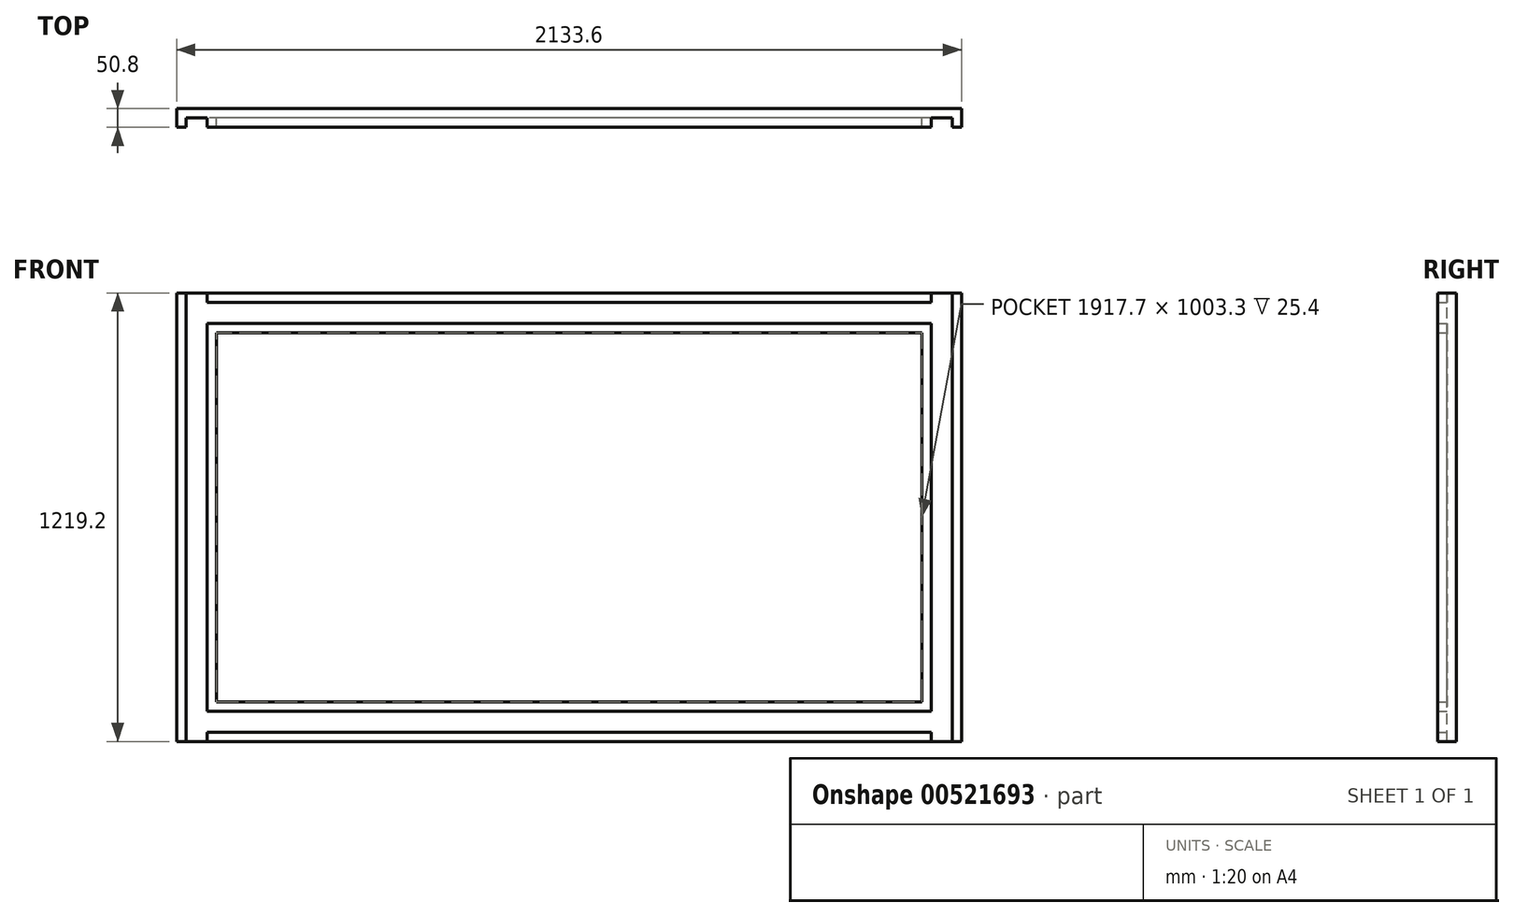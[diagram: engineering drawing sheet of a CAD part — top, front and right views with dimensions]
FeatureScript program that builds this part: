
annotation { "Feature Type Name" : "Feature", "Feature Type Description" : "" }
export const myFeature = defineFeature(function(context is Context, id is Id, definition is map)
    precondition{}
    {
        {
            var Q0;
            Q0=qCreatedBy(makeId("Front.planeOp"),FACE);
            var sketch = newSketch(context, id + "F0", { "sketchPlane" : qUnion([Q0])});
            skLineSegment(sketch, "E0.bottom", {"start": v(0, 0) * mm, "end": v(2133.6, 0) * mm});
            skLineSegment(sketch, "E0.top", {"start": v(0, 1219.2) * mm, "end": v(2133.6, 1219.2) * mm});
            skLineSegment(sketch, "E0.left", {"start": v(0, 0) * mm, "end": v(0, 1219.2) * mm});
            skLineSegment(sketch, "E0.right", {"start": v(2133.6, 0) * mm, "end": v(2133.6, 1219.2) * mm});
            skSolve(sketch);
        }
        {
            var Q0;
            Q0 = qSketchRegion(id + "F0", true);
            extrude(context, id + "F1", {"entities" : qUnion([Q0]), "depth" : 25.4 * mm, "offsetDistance" : 25.4 * mm});
        }
        {
            var Q0;
            Q0=makeQuery(id+"F1.opExtrude","CAP_FACE",FACE,{"disambiguationData":[OSD([sQuery(id+"F0.wireOp",EDGE,"E0.bottom"),sQuery(id+"F0.wireOp",EDGE,"E0.top"),sQuery(id+"F0.wireOp",EDGE,"E0.left"),sQuery(id+"F0.wireOp",EDGE,"E0.right")])],"isStart":false});
            var sketch = newSketch(context, id + "F2", { "sketchPlane" : qUnion([Q0])});
            skLineSegment(sketch, "E1.bottom", {"start": v(2051.05, 1219.2) * mm, "end": v(82.55, 1219.2) * mm});
            skLineSegment(sketch, "E1.top", {"start": v(2051.05, 1193.8) * mm, "end": v(82.55, 1193.8) * mm});
            skLineSegment(sketch, "E1.left", {"start": v(2051.05, 1219.2) * mm, "end": v(2051.05, 1193.8) * mm});
            skLineSegment(sketch, "E1.right", {"start": v(82.55, 1219.2) * mm, "end": v(82.55, 1193.8) * mm});
            skSolve(sketch);
        }
        {
            var Q0;
            Q0 = qSketchRegion(id + "F2", true);
            extrude(context, id + "F3", {"entities" : qUnion([Q0]), "operationType" : NewBodyOperationType.ADD, "depth" : 25.4 * mm, "offsetDistance" : 25.4 * mm});
        }
        {
            var Q0;
            Q0=makeQuery(id+"F1.opExtrude","CAP_FACE",FACE,{"disambiguationData":[OSD([sQuery(id+"F0.wireOp",EDGE,"E0.bottom"),sQuery(id+"F0.wireOp",EDGE,"E0.top"),sQuery(id+"F0.wireOp",EDGE,"E0.left"),sQuery(id+"F0.wireOp",EDGE,"E0.right")])],"isStart":false});
            var sketch = newSketch(context, id + "F4", { "sketchPlane" : qUnion([Q0])});
            skLineSegment(sketch, "E2.bottom", {"start": v(82.55, 0) * mm, "end": v(2051.05, 0) * mm});
            skLineSegment(sketch, "E2.top", {"start": v(82.55, 25.4) * mm, "end": v(2051.05, 25.4) * mm});
            skLineSegment(sketch, "E2.left", {"start": v(82.55, 0) * mm, "end": v(82.55, 25.4) * mm});
            skLineSegment(sketch, "E2.right", {"start": v(2051.05, 0) * mm, "end": v(2051.05, 25.4) * mm});
            skSolve(sketch);
        }
        {
            var Q0;
            Q0 = qSketchRegion(id + "F4", true);
            extrude(context, id + "F5", {"entities" : qUnion([Q0]), "operationType" : NewBodyOperationType.ADD, "depth" : 25.4 * mm, "offsetDistance" : 25.4 * mm});
        }
        {
            var Q0;
            Q0=makeQuery(id+"F1.opExtrude","CAP_FACE",FACE,{"disambiguationData":[OSD([sQuery(id+"F0.wireOp",EDGE,"E0.bottom"),sQuery(id+"F0.wireOp",EDGE,"E0.top"),sQuery(id+"F0.wireOp",EDGE,"E0.left"),sQuery(id+"F0.wireOp",EDGE,"E0.right")])],"isStart":false});
            var sketch = newSketch(context, id + "F6", { "sketchPlane" : qUnion([Q0])});
            skLineSegment(sketch, "E3.bottom", {"start": v(0, 1219.2) * mm, "end": v(25.4, 1219.2) * mm});
            skLineSegment(sketch, "E3.top", {"start": v(0, 0) * mm, "end": v(25.4, 0) * mm});
            skLineSegment(sketch, "E3.left", {"start": v(0, 1219.2) * mm, "end": v(0, 0) * mm});
            skLineSegment(sketch, "E3.right", {"start": v(25.4, 1219.2) * mm, "end": v(25.4, 0) * mm});
            skSolve(sketch);
        }
        {
            var Q0;
            Q0 = qSketchRegion(id + "F6", true);
            extrude(context, id + "F7", {"entities" : qUnion([Q0]), "operationType" : NewBodyOperationType.ADD, "depth" : 25.4 * mm, "offsetDistance" : 25.4 * mm});
        }
        {
            var Q0;
            Q0=makeQuery(id+"F1.opExtrude","CAP_FACE",FACE,{"disambiguationData":[OSD([sQuery(id+"F0.wireOp",EDGE,"E0.bottom"),sQuery(id+"F0.wireOp",EDGE,"E0.top"),sQuery(id+"F0.wireOp",EDGE,"E0.left"),sQuery(id+"F0.wireOp",EDGE,"E0.right")])],"isStart":false});
            var sketch = newSketch(context, id + "F8", { "sketchPlane" : qUnion([Q0])});
            skLineSegment(sketch, "E4.bottom", {"start": v(2133.6, 0) * mm, "end": v(2108.2, 0) * mm});
            skLineSegment(sketch, "E4.top", {"start": v(2133.6, 1219.2) * mm, "end": v(2108.2, 1219.2) * mm});
            skLineSegment(sketch, "E4.left", {"start": v(2133.6, 0) * mm, "end": v(2133.6, 1219.2) * mm});
            skLineSegment(sketch, "E4.right", {"start": v(2108.2, 0) * mm, "end": v(2108.2, 1219.2) * mm});
            skSolve(sketch);
        }
        {
            var Q0;
            Q0 = qSketchRegion(id + "F8", true);
            extrude(context, id + "F9", {"entities" : qUnion([Q0]), "operationType" : NewBodyOperationType.ADD, "depth" : 25.4 * mm, "offsetDistance" : 25.4 * mm});
        }
        {
            var Q0;
            Q0=makeQuery(id+"F1.opExtrude","CAP_FACE",FACE,{"disambiguationData":[OSD([sQuery(id+"F0.wireOp",EDGE,"E0.bottom"),sQuery(id+"F0.wireOp",EDGE,"E0.top"),sQuery(id+"F0.wireOp",EDGE,"E0.left"),sQuery(id+"F0.wireOp",EDGE,"E0.right")])],"isStart":false});
            var sketch = newSketch(context, id + "F10", { "sketchPlane" : qUnion([Q0])});
            skLineSegment(sketch, "E5.bottom", {"start": v(2051.05, 1136.65) * mm, "end": v(82.55, 1136.65) * mm});
            skLineSegment(sketch, "E5.top", {"start": v(2051.05, 1111.25) * mm, "end": v(82.55, 1111.25) * mm});
            skLineSegment(sketch, "E5.left", {"start": v(2051.05, 1136.65) * mm, "end": v(2051.05, 1111.25) * mm});
            skLineSegment(sketch, "E5.right", {"start": v(82.55, 1136.65) * mm, "end": v(82.55, 1111.25) * mm});
            skSolve(sketch);
        }
        {
            var Q0;
            Q0 = qSketchRegion(id + "F10", true);
            extrude(context, id + "F11", {"entities" : qUnion([Q0]), "operationType" : NewBodyOperationType.ADD, "depth" : 25.4 * mm, "offsetDistance" : 25.4 * mm});
        }
        {
            var Q0;
            Q0=makeQuery(id+"F1.opExtrude","CAP_FACE",FACE,{"disambiguationData":[OSD([sQuery(id+"F0.wireOp",EDGE,"E0.bottom"),sQuery(id+"F0.wireOp",EDGE,"E0.top"),sQuery(id+"F0.wireOp",EDGE,"E0.left"),sQuery(id+"F0.wireOp",EDGE,"E0.right")])],"isStart":false});
            var sketch = newSketch(context, id + "F12", { "sketchPlane" : qUnion([Q0])});
            skLineSegment(sketch, "E6.bottom", {"start": v(82.55, 82.55) * mm, "end": v(2051.05, 82.55) * mm});
            skLineSegment(sketch, "E6.top", {"start": v(82.55, 107.95) * mm, "end": v(2051.05, 107.95) * mm});
            skLineSegment(sketch, "E6.left", {"start": v(82.55, 82.55) * mm, "end": v(82.55, 107.95) * mm});
            skLineSegment(sketch, "E6.right", {"start": v(2051.05, 82.55) * mm, "end": v(2051.05, 107.95) * mm});
            skSolve(sketch);
        }
        {
            var Q0;
            Q0 = qSketchRegion(id + "F12", true);
            extrude(context, id + "F13", {"entities" : qUnion([Q0]), "operationType" : NewBodyOperationType.ADD, "depth" : 25.4 * mm, "offsetDistance" : 25.4 * mm});
        }
        {
            var Q0;
            Q0=makeQuery(id+"F1.opExtrude","CAP_FACE",FACE,{"disambiguationData":[OSD([sQuery(id+"F0.wireOp",EDGE,"E0.bottom"),sQuery(id+"F0.wireOp",EDGE,"E0.top"),sQuery(id+"F0.wireOp",EDGE,"E0.left"),sQuery(id+"F0.wireOp",EDGE,"E0.right")])],"isStart":false});
            var sketch = newSketch(context, id + "F14", { "sketchPlane" : qUnion([Q0])});
            skLineSegment(sketch, "E7.bottom", {"start": v(2051.05, 107.95) * mm, "end": v(2025.65, 107.95) * mm});
            skLineSegment(sketch, "E7.top", {"start": v(2051.05, 1111.25) * mm, "end": v(2025.65, 1111.25) * mm});
            skLineSegment(sketch, "E7.left", {"start": v(2051.05, 107.95) * mm, "end": v(2051.05, 1111.25) * mm});
            skLineSegment(sketch, "E7.right", {"start": v(2025.65, 107.95) * mm, "end": v(2025.65, 1111.25) * mm});
            skSolve(sketch);
        }
        {
            var Q0;
            Q0 = qSketchRegion(id + "F14", true);
            extrude(context, id + "F15", {"entities" : qUnion([Q0]), "operationType" : NewBodyOperationType.ADD, "depth" : 25.4 * mm, "offsetDistance" : 25.4 * mm});
        }
        {
            var Q0;
            Q0=makeQuery(id+"F1.opExtrude","CAP_FACE",FACE,{"disambiguationData":[OSD([sQuery(id+"F0.wireOp",EDGE,"E0.bottom"),sQuery(id+"F0.wireOp",EDGE,"E0.top"),sQuery(id+"F0.wireOp",EDGE,"E0.left"),sQuery(id+"F0.wireOp",EDGE,"E0.right")])],"isStart":false});
            var sketch = newSketch(context, id + "F16", { "sketchPlane" : qUnion([Q0])});
            skLineSegment(sketch, "E8.bottom", {"start": v(82.55, 107.95) * mm, "end": v(107.95, 107.95) * mm});
            skLineSegment(sketch, "E8.top", {"start": v(82.55, 1111.25) * mm, "end": v(107.95, 1111.25) * mm});
            skLineSegment(sketch, "E8.left", {"start": v(82.55, 107.95) * mm, "end": v(82.55, 1111.25) * mm});
            skLineSegment(sketch, "E8.right", {"start": v(107.95, 107.95) * mm, "end": v(107.95, 1111.25) * mm});
            skSolve(sketch);
        }
        {
            var Q0;
            Q0 = qSketchRegion(id + "F16", true);
            extrude(context, id + "F17", {"entities" : qUnion([Q0]), "operationType" : NewBodyOperationType.ADD, "depth" : 25.4 * mm, "offsetDistance" : 25.4 * mm});
        }
    });
